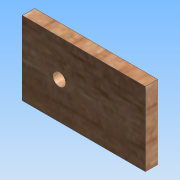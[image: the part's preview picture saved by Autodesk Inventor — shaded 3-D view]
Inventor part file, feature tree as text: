
AUTODESK INVENTOR PART (.ipt)
format: ipt  version: 2015 (Build 190159000, 159)  size: 99,840 bytes
history: native  units: mm
features: extrude x1, sketch x1
ambient origin geometry x8: Origin, YZ Plane, XZ Plane, XY Plane, X Axis, Y Axis, Z Axis, Center Point
bodies: Body1 (feature_tree)
feature tree (2):
  extrude  "Extrusion2"  Depth=50.0mm
  sketch  "Sketch1"  dims[d2=30.0mm d3=50.0mm d4=5.2mm d5=5.0mm d6=0.0mm d7=15.0mm]
